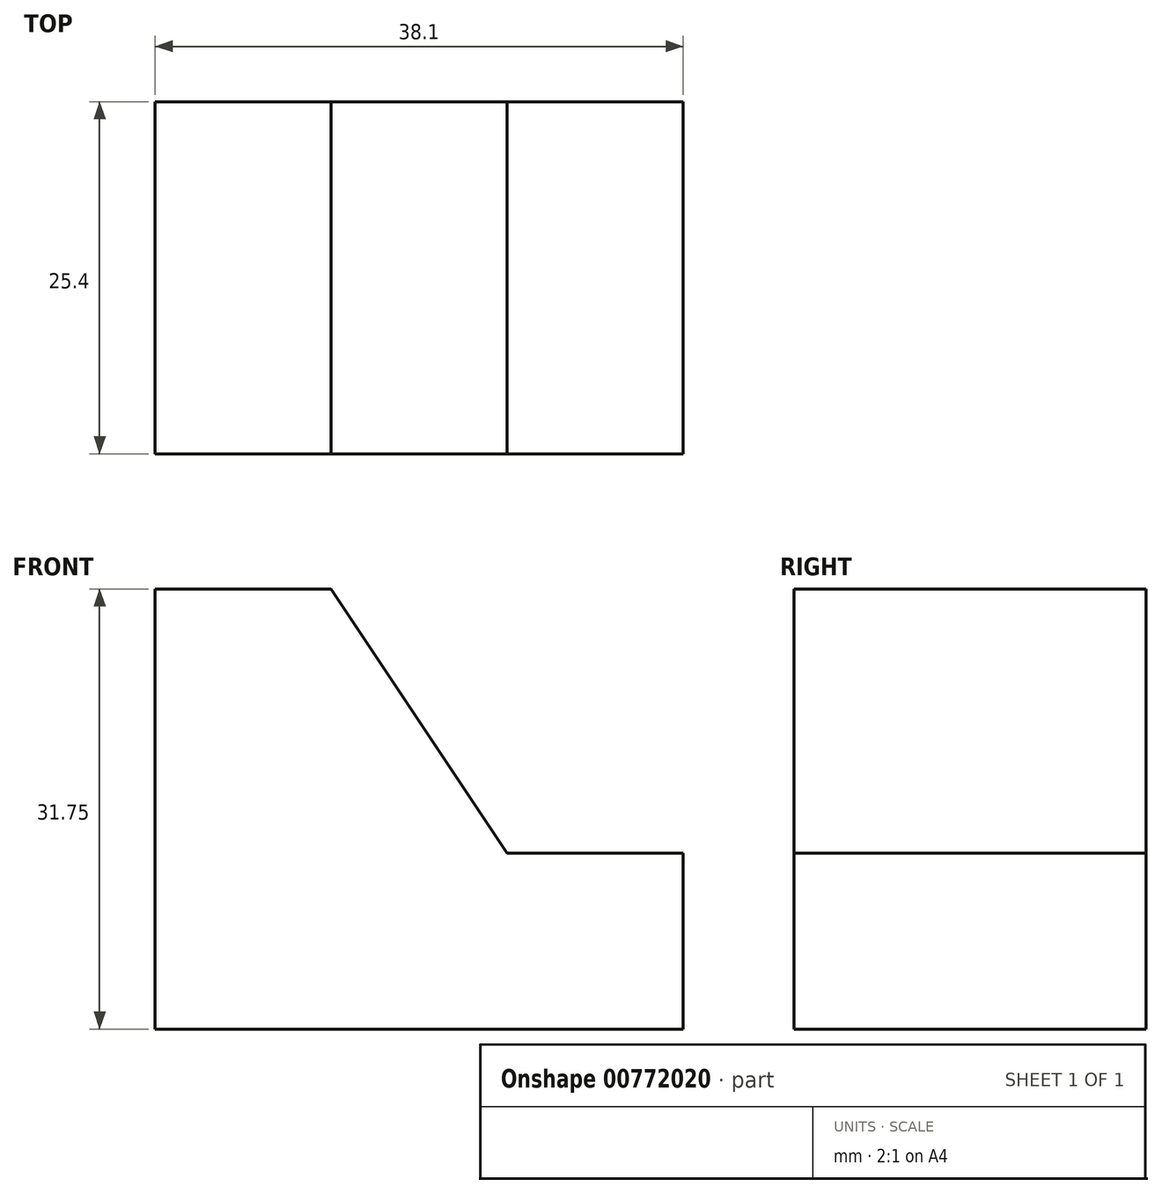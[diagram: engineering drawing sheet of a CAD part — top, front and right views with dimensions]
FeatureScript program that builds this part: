
annotation { "Feature Type Name" : "Feature", "Feature Type Description" : "" }
export const myFeature = defineFeature(function(context is Context, id is Id, definition is map)
    precondition{}
    {
        {
            var Q0;
            Q0=qCreatedBy(makeId("Front.planeOp"),FACE);
            var sketch = newSketch(context, id + "F0", { "sketchPlane" : qUnion([Q0])});
            skLineSegment(sketch, "E0", {"start": v(0, 0) * mm, "end": v(38.1, 0) * mm});
            skLineSegment(sketch, "E1", {"start": v(38.1, 0) * mm, "end": v(38.1, 12.7) * mm});
            skLineSegment(sketch, "E2", {"start": v(0, 0) * mm, "end": v(0, 31.75) * mm});
            skLineSegment(sketch, "E3", {"start": v(0, 31.75) * mm, "end": v(12.7, 31.75) * mm});
            skLineSegment(sketch, "E4", {"start": v(38.1, 12.7) * mm, "end": v(25.4, 12.7) * mm});
            skLineSegment(sketch, "E5", {"start": v(25.4, 12.7) * mm, "end": v(12.7, 31.75) * mm});
            skSolve(sketch);
        }
        {
            var Q0;
            Q0 = qSketchRegion(id + "F0", true);
            extrude(context, id + "F1", {"entities" : qUnion([Q0]), "depth" : 25.4 * mm, "offsetDistance" : 25.4 * mm});
        }
    });
